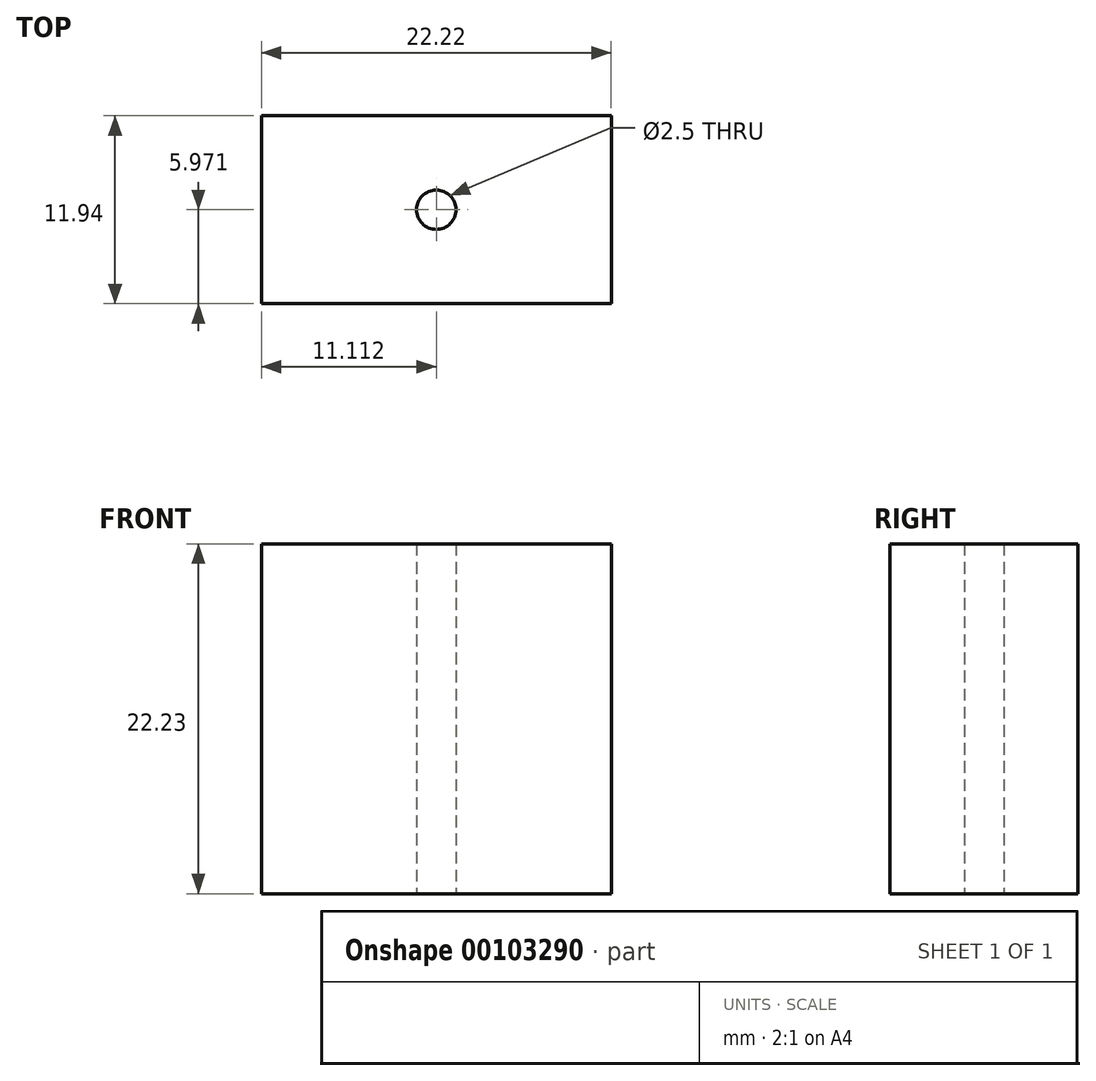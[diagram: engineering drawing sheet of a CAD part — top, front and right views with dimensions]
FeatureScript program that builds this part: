
annotation { "Feature Type Name" : "Feature", "Feature Type Description" : "" }
export const myFeature = defineFeature(function(context is Context, id is Id, definition is map)
    precondition{}
    {
        {
            var Q0;
            Q0=qCreatedBy(makeId("Front.planeOp"),FACE);
            var sketch = newSketch(context, id + "F0", { "sketchPlane" : qUnion([Q0])});
            skLineSegment(sketch, "E0.bottom", {"start": v(1.32, 0) * mm, "end": v(23.54, 0) * mm});
            skLineSegment(sketch, "E0.top", {"start": v(1.32, 22.23) * mm, "end": v(23.54, 22.23) * mm});
            skLineSegment(sketch, "E0.left", {"start": v(1.32, 0) * mm, "end": v(1.32, 22.23) * mm});
            skLineSegment(sketch, "E0.right", {"start": v(23.54, 0) * mm, "end": v(23.54, 22.23) * mm});
            skSolve(sketch);
        }
        {
            var Q0;
            Q0=makeQuery(id+"F0.imprint","IMPRINT",FACE,{"disambiguationData":[TD([[makeQuery(id+"F0.imprint","IMPRINT",EDGE,{"derivedFrom":sQuery(id+"F0.wireOp",EDGE,"E0.bottom")}),1.0]])]});
            extrude(context, id + "F1", {"entities" : qUnion([Q0]), "depth" : 11.94 * mm});
        }
        {
            var Q0;
            Q0=makeQuery(id+"F1.opExtrude","SWEPT_FACE",FACE,{"disambiguationData":[OSD([sQuery(id+"F0.wireOp",EDGE,"E0.bottom")])]});
            var sketch = newSketch(context, id + "F2", { "sketchPlane" : qUnion([Q0])});
            skLineSegment(sketch, "E1", {"start": v(1.32, 5.97) * mm, "end": v(12.43, 5.97) * mm});
            skPoint(sketch, "E1.endSnap0", {"position": v(1.32, 5.97) * mm});
            skCircle(sketch, "E2", {"center": v(12.43, 5.97) * mm, "radius": 1.25 * mm});
            skSolve(sketch);
        }
        {
            var Q0;
            Q0=makeQuery(id+"F2.imprint","IMPRINT",FACE,{"disambiguationData":[TD([[makeQuery(id+"F2.imprint","IMPRINT",EDGE,{"derivedFrom":sQuery(id+"F2.wireOp",EDGE,"E2")}),1.0]])]});
            extrude(context, id + "F3", {"entities" : qUnion([Q0]), "operationType" : NewBodyOperationType.REMOVE, "oppositeDirection" : true, "depth" : 25.4 * mm});
        }
    });
